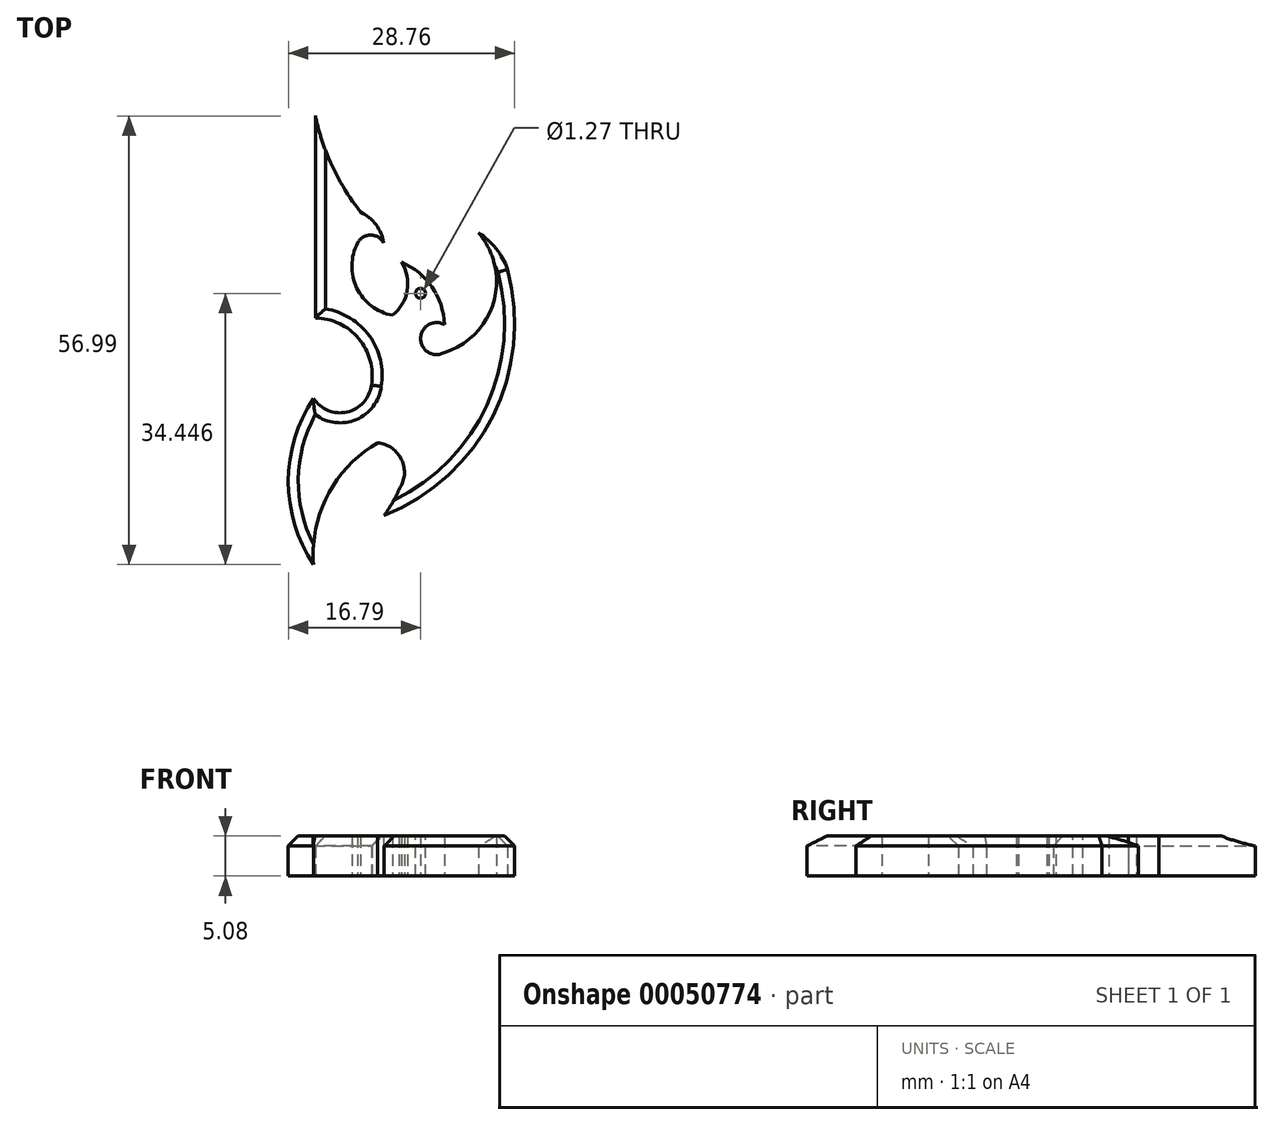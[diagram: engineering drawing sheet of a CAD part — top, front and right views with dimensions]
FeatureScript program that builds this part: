
annotation { "Feature Type Name" : "Feature", "Feature Type Description" : "" }
export const myFeature = defineFeature(function(context is Context, id is Id, definition is map)
    precondition{}
    {
        {
            var Q0;
            Q0=qCreatedBy(makeId("Top.planeOp"),FACE);
            var sketch = newSketch(context, id + "F0", { "sketchPlane" : qUnion([Q0])});
            skArc(sketch, "E0", {"start": v(35.81, 50.65) * mm, "mid": v(34.16, 51.67) * mm, "end": v(32.51, 50.65) * mm});
            skArc(sketch, "E1", {"start": v(32.51, 50.65) * mm, "mid": v(32.4, 44.95) * mm, "end": v(36.93, 41.47) * mm});
            skArc(sketch, "E2", {"start": v(36.93, 41.47) * mm, "mid": v(38.8, 44.62) * mm, "end": v(38.1, 48.21) * mm});
            skArc(sketch, "E3", {"start": v(43.52, 40.3) * mm, "mid": v(41.96, 45.05) * mm, "end": v(38.1, 48.21) * mm});
            skArc(sketch, "E4", {"start": v(35.81, 50.65) * mm, "mid": v(34.84, 52.97) * mm, "end": v(32.9, 54.58) * mm});
            skArc(sketch, "E5", {"start": v(27.13, 66.81) * mm, "mid": v(29.3, 60.36) * mm, "end": v(32.9, 54.58) * mm});
            skLineSegment(sketch, "E6", {"start": v(27.13, 66.81) * mm, "end": v(27.13, 41.13) * mm});
            skArc(sketch, "E7", {"start": v(26.9, 30.93) * mm, "mid": v(23.7, 20.38) * mm, "end": v(26.9, 9.82) * mm});
            skArc(sketch, "E8", {"start": v(35.05, 25.27) * mm, "mid": v(28.74, 18.73) * mm, "end": v(26.9, 9.82) * mm});
            skArc(sketch, "E9", {"start": v(37.78, 19.37) * mm, "mid": v(38.1, 23.1) * mm, "end": v(35.05, 25.27) * mm});
            skArc(sketch, "E10", {"start": v(35.87, 16.05) * mm, "mid": v(36.92, 17.66) * mm, "end": v(37.78, 19.37) * mm});
            skArc(sketch, "E11", {"start": v(35.87, 16.05) * mm, "mid": v(49.68, 28.69) * mm, "end": v(51.54, 47.31) * mm});
            skArc(sketch, "E12", {"start": v(43.52, 40.3) * mm, "mid": v(40.5, 38.51) * mm, "end": v(43.52, 36.73) * mm});
            skArc(sketch, "E13", {"start": v(43.52, 36.73) * mm, "mid": v(49.78, 43.19) * mm, "end": v(47.84, 51.97) * mm});
            skArc(sketch, "E14", {"start": v(51.54, 47.31) * mm, "mid": v(50.1, 49.96) * mm, "end": v(47.84, 51.97) * mm});
            skArc(sketch, "E15", {"start": v(34.25, 32.62) * mm, "mid": v(32.65, 38.51) * mm, "end": v(27.13, 41.13) * mm});
            skArc(sketch, "E16", {"start": v(26.9, 30.93) * mm, "mid": v(31.17, 29.19) * mm, "end": v(34.25, 32.62) * mm});
            skSolve(sketch);
        }
        {
            var Q0;
            Q0 = qSketchRegion(id + "F0", true);
            extrude(context, id + "F1", {"entities" : qUnion([Q0]), "depth" : 5.08 * mm});
        }
        {
            var Q0;
            Q0=makeQuery(id+"F1.opExtrude","CAP_EDGE",EDGE,{"disambiguationData":[OSD([sQuery(id+"F0.wireOp",EDGE,"E6")])],"isStart":false});
            var Q1;
            Q1=makeQuery(id+"F1.opExtrude","CAP_EDGE",EDGE,{"disambiguationData":[OSD([sQuery(id+"F0.wireOp",EDGE,"E15")])],"isStart":false});
            var Q2;
            Q2=makeQuery(id+"F1.opExtrude","CAP_EDGE",EDGE,{"disambiguationData":[OSD([sQuery(id+"F0.wireOp",EDGE,"E7")])],"isStart":false});
            var Q3;
            Q3=makeQuery(id+"F1.opExtrude","CAP_EDGE",EDGE,{"disambiguationData":[OSD([sQuery(id+"F0.wireOp",EDGE,"E11")])],"isStart":false});
            var Q4;
            Q4=makeQuery(id+"F1.opExtrude","CAP_EDGE",EDGE,{"disambiguationData":[OSD([sQuery(id+"F0.wireOp",EDGE,"E14")])],"isStart":false});
            chamfer(context, id + "F2", {"entities" : qUnion([Q0, Q1, Q2, Q3, Q4]), "width" : 1.27 * mm, "tangentPropagation" : true});
        }
        {
            var Q0;
            Q0=makeQuery(id+"F2.opChamfer","SPLIT",FACE,{"disambiguationData":[OD(2.0)],"derivedFrom":makeQuery(id+"F1.opExtrude","CAP_FACE",FACE,{"disambiguationData":[OSD([sQuery(id+"F0.wireOp",EDGE,"E0"),sQuery(id+"F0.wireOp",EDGE,"E1"),sQuery(id+"F0.wireOp",EDGE,"E2"),sQuery(id+"F0.wireOp",EDGE,"E3"),sQuery(id+"F0.wireOp",EDGE,"E4"),sQuery(id+"F0.wireOp",EDGE,"E5"),sQuery(id+"F0.wireOp",EDGE,"E6"),sQuery(id+"F0.wireOp",EDGE,"E7"),sQuery(id+"F0.wireOp",EDGE,"E8"),sQuery(id+"F0.wireOp",EDGE,"E9"),sQuery(id+"F0.wireOp",EDGE,"E10"),sQuery(id+"F0.wireOp",EDGE,"E11"),sQuery(id+"F0.wireOp",EDGE,"E12"),sQuery(id+"F0.wireOp",EDGE,"E13"),sQuery(id+"F0.wireOp",EDGE,"E14"),sQuery(id+"F0.wireOp",EDGE,"E15"),sQuery(id+"F0.wireOp",EDGE,"E16")])],"isStart":false})});
            var sketch = newSketch(context, id + "F3", { "sketchPlane" : qUnion([Q0])});
            skPoint(sketch, "E17", {"position": v(40.49, 44.27) * mm});
            skSolve(sketch);
        }
        {
            var Q0;
            Q0=sQuery(id+"F3.wireOp",VERTEX,"E17");
            var Q1;
            Q1=makeQuery(id+"F1.opExtrude","SWEPT_BODY",BODY,{"disambiguationData":[OSD([sQuery(id+"F0.wireOp",EDGE,"E0"),sQuery(id+"F0.wireOp",EDGE,"E1"),sQuery(id+"F0.wireOp",EDGE,"E2"),sQuery(id+"F0.wireOp",EDGE,"E3"),sQuery(id+"F0.wireOp",EDGE,"E4"),sQuery(id+"F0.wireOp",EDGE,"E5"),sQuery(id+"F0.wireOp",EDGE,"E6"),sQuery(id+"F0.wireOp",EDGE,"E7"),sQuery(id+"F0.wireOp",EDGE,"E8"),sQuery(id+"F0.wireOp",EDGE,"E9"),sQuery(id+"F0.wireOp",EDGE,"E10"),sQuery(id+"F0.wireOp",EDGE,"E11"),sQuery(id+"F0.wireOp",EDGE,"E12"),sQuery(id+"F0.wireOp",EDGE,"E13"),sQuery(id+"F0.wireOp",EDGE,"E14"),sQuery(id+"F0.wireOp",EDGE,"E15"),sQuery(id+"F0.wireOp",EDGE,"E16")])]});
            hole(context, id + "F4", {"style" : HoleStyle.SIMPLE, "holeDiameter" : 1.27 * mm, "endStyle" : HoleEndStyle.THROUGH, "locations" : qUnion([Q0]), "scope" : qUnion([Q1])});
        }
    });
